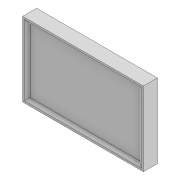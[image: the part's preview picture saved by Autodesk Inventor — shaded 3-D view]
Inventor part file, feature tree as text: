
AUTODESK INVENTOR PART (.ipt)
format: ipt  version: 2020 (Build 240168000, 168)  size: 98,816 bytes
history: native  units: mm
features: extrude x2, sketch x2, fillet x1
ambient origin geometry x8: Origin, YZ Plane, XZ Plane, XY Plane, X Axis, Y Axis, Z Axis, Center Point
bodies: Volumenkörper1 (feature_tree)
feature tree (5):
  extrude  "Extrusion1"  Depth=130.0mm
  extrude  "Extrusion2"  Depth=3.0mm
  fillet  "Rundung1"  Radius=5.0mm
  sketch  "Skizze2"  dims[d0=80.0mm d1=130.0mm]
  sketch  "Skizze3"  dims[d2=15.0mm d3=0.0mm d4=5.0mm d5=5.0mm d6=5.0mm d7=5.0mm d8=3.0mm d9=0.0mm d10=3.0mm]
